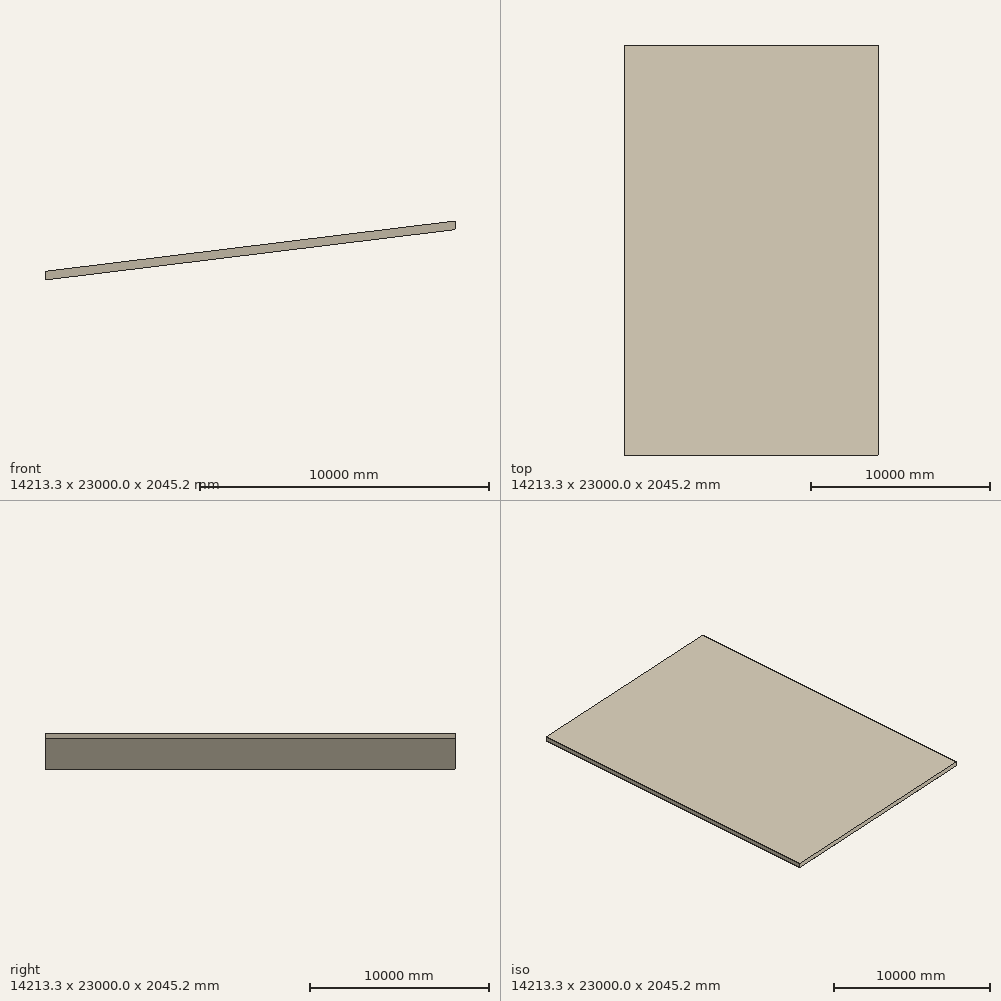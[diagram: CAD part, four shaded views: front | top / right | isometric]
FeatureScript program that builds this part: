
annotation { "Feature Type Name" : "Feature", "Feature Type Description" : "" }
export const myFeature = defineFeature(function(context is Context, id is Id, definition is map)
    precondition{}
    {
        {
            var Q0;
            Q0=qCreatedBy(makeId("Front.planeOp"),FACE);
            var sketch = newSketch(context, id + "F0", { "sketchPlane" : qUnion([Q0])});
            skLineSegment(sketch, "E0", {"start": v(0, 0) * mm, "end": v(0, 300) * mm});
            skLineSegment(sketch, "E1", {"start": v(0, 300) * mm, "end": v(14213.26, 2045.17) * mm});
            skLineSegment(sketch, "E2", {"start": v(14213.26, 2045.17) * mm, "end": v(14213.26, 1745.17) * mm});
            skLineSegment(sketch, "E3", {"start": v(14213.26, 1745.17) * mm, "end": v(0, 0) * mm});
            skSolve(sketch);
        }
        {
            var Q0;
            Q0=makeQuery(id+"F0.imprint","IMPRINT",FACE,{"disambiguationData":[TD([[makeQuery(id+"F0.imprint","IMPRINT",EDGE,{"derivedFrom":sQuery(id+"F0.wireOp",EDGE,"E0")}),-1.0]])]});
            extrude(context, id + "F1", {"entities" : qUnion([Q0]), "depth" : 23000 * mm});
        }
    });
